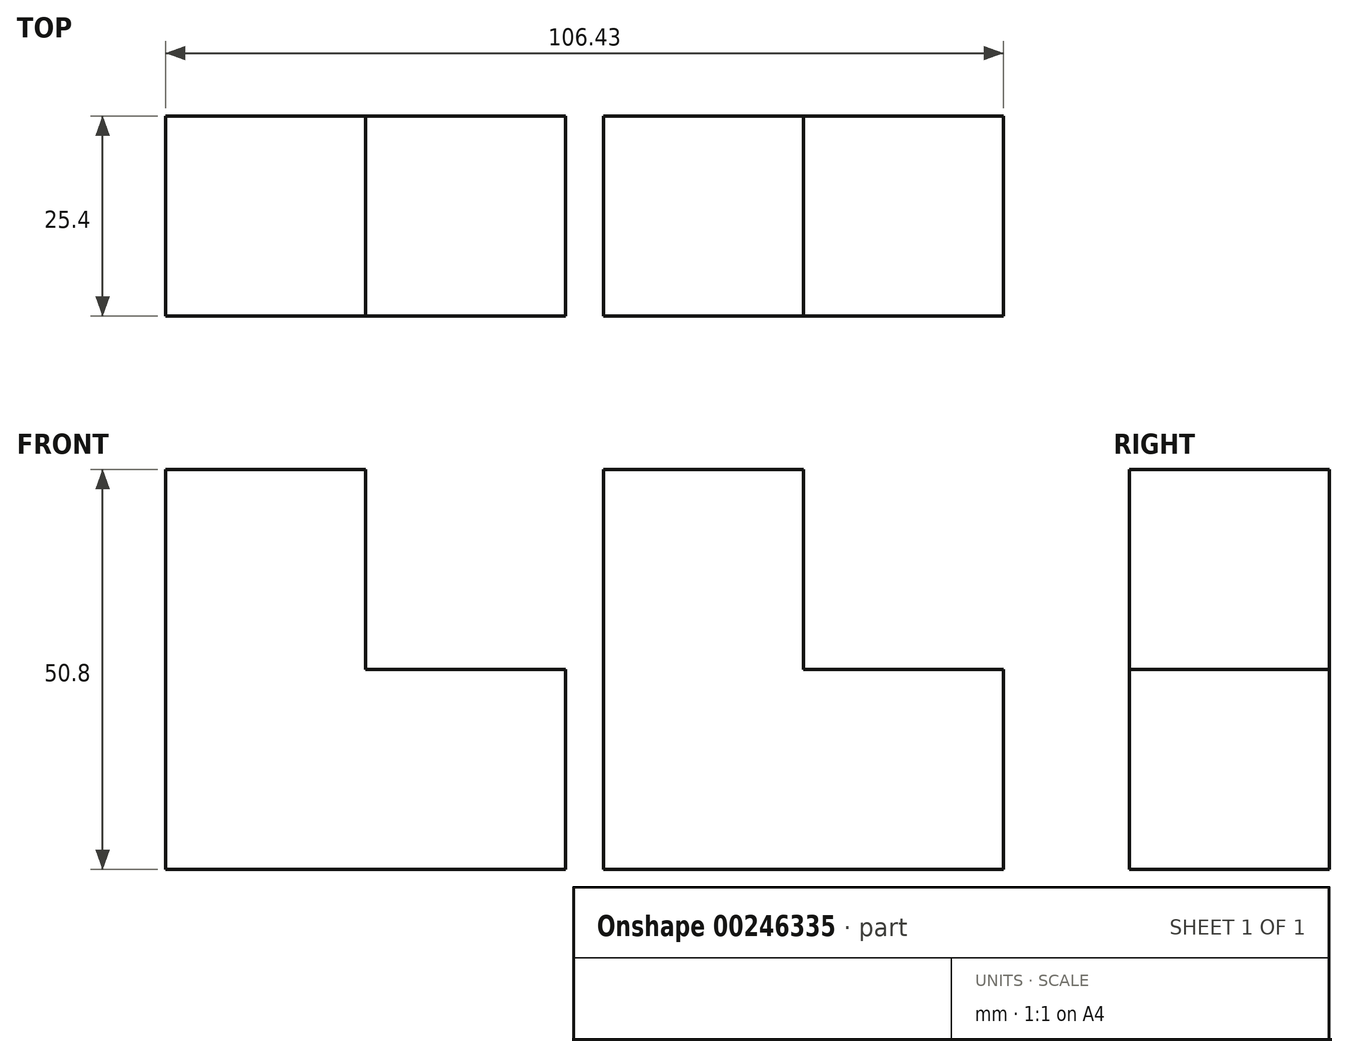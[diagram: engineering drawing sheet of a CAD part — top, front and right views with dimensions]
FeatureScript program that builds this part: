
annotation { "Feature Type Name" : "Feature", "Feature Type Description" : "" }
export const myFeature = defineFeature(function(context is Context, id is Id, definition is map)
    precondition{}
    {
        {
            var Q0;
            Q0=qCreatedBy(makeId("Front.planeOp"),FACE);
            var sketch = newSketch(context, id + "F0", { "sketchPlane" : qUnion([Q0])});
            skLineSegment(sketch, "E0", {"start": v(-26.97, 40.62) * mm, "end": v(-26.97, -10.18) * mm});
            skLineSegment(sketch, "E1", {"start": v(-26.97, -10.18) * mm, "end": v(23.83, -10.18) * mm});
            skLineSegment(sketch, "E2", {"start": v(23.83, -10.18) * mm, "end": v(23.83, 15.22) * mm});
            skLineSegment(sketch, "E3", {"start": v(23.83, 15.22) * mm, "end": v(-1.57, 15.22) * mm});
            skLineSegment(sketch, "E4", {"start": v(-1.57, 15.22) * mm, "end": v(-1.57, 40.62) * mm});
            skLineSegment(sketch, "E5", {"start": v(-1.57, 40.62) * mm, "end": v(-26.97, 40.62) * mm});
            skSolve(sketch);
        }
        {
            var Q0;
            Q0 = qSketchRegion(id + "F0", true);
            extrude(context, id + "F1", {"entities" : qUnion([Q0]), "depth" : 25.4 * mm});
        }
        {
            var Q0;
            Q0=makeQuery(id+"F1.opExtrude","SWEPT_BODY",BODY,{"disambiguationData":[OSD([sQuery(id+"F0.wireOp",EDGE,"E0"),sQuery(id+"F0.wireOp",EDGE,"E1"),sQuery(id+"F0.wireOp",EDGE,"E2"),sQuery(id+"F0.wireOp",EDGE,"E3"),sQuery(id+"F0.wireOp",EDGE,"E4"),sQuery(id+"F0.wireOp",EDGE,"E5")])]});
            transform(context, id + "F2", {"entities" : qUnion([Q0]), "transformType" : TransformType.TRANSLATION_3D, "dx" : 55.63 * mm, "dy" : 0 * mm, "dz" : 0 * mm, "makeCopy" : true});
        }
    });
